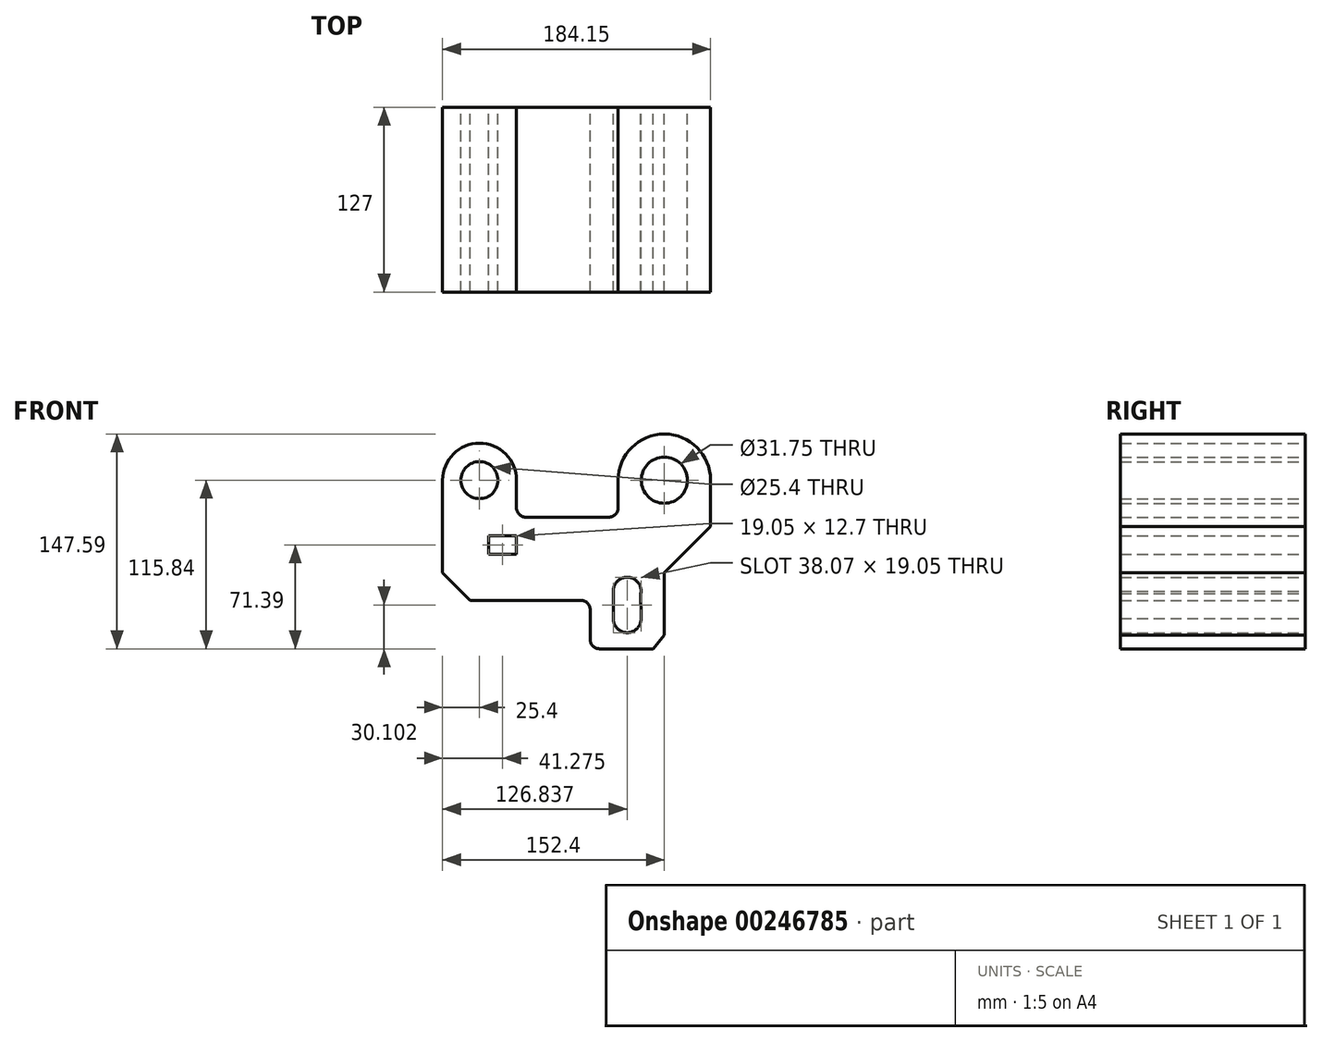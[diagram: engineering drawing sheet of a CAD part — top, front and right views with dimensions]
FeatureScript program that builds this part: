
annotation { "Feature Type Name" : "Feature", "Feature Type Description" : "" }
export const myFeature = defineFeature(function(context is Context, id is Id, definition is map)
    precondition{}
    {
        {
            var Q0;
            Q0=qCreatedBy(makeId("Front.planeOp"),FACE);
            var sketch = newSketch(context, id + "F0", { "sketchPlane" : qUnion([Q0])});
            skCircle(sketch, "E0", {"center": v(0, 0) * mm, "radius": 15.88 * mm});
            skArc(sketch, "E1", {"start": v(31.75, 0) * mm, "mid": v(0, 31.75) * mm, "end": v(-31.75, 0) * mm});
            skLineSegment(sketch, "E2", {"start": v(31.75, 0) * mm, "end": v(31.75, -31.75) * mm});
            skLineSegment(sketch, "E3", {"start": v(31.75, -31.75) * mm, "end": v(62.44, -31.75) * mm, "construction": true});
            skLineSegment(sketch, "E4", {"start": v(0, 0) * mm, "end": v(63.42, 0) * mm, "construction": true});
            skLineSegment(sketch, "E5", {"start": v(70.44, -114.3) * mm, "end": v(0, -114.3) * mm, "construction": true});
            skLineSegment(sketch, "E6", {"start": v(84.52, -63.5) * mm, "end": v(0, -63.5) * mm, "construction": true});
            skArc(sketch, "E7", {"start": v(-101.6, 0) * mm, "mid": v(-127, 25.4) * mm, "end": v(-152.4, 0) * mm});
            skCircle(sketch, "E8", {"center": v(-127, 0) * mm, "radius": 12.7 * mm});
            skLineSegment(sketch, "E9", {"start": v(-95.25, -25.4) * mm, "end": v(-38.1, -25.4) * mm});
            skLineSegment(sketch, "E10", {"start": v(-101.6, 0) * mm, "end": v(-101.6, -19.05) * mm});
            skLineSegment(sketch, "E11", {"start": v(-31.75, 0) * mm, "end": v(-31.75, -19.05) * mm});
            skLineSegment(sketch, "E12", {"start": v(31.75, -31.75) * mm, "end": v(-0.04, -63.54) * mm});
            skPoint(sketch, "E13.visualSharp", {"position": v(-31.75, -25.4) * mm});
            skArc(sketch, "E13.filletArc", {"start": v(-38.1, -25.4) * mm, "mid": v(-33.6, -23.54) * mm, "end": v(-31.75, -19.05) * mm});
            skPoint(sketch, "E14.visualSharp", {"position": v(-101.6, -25.4) * mm});
            skArc(sketch, "E14.filletArc", {"start": v(-101.6, -19.05) * mm, "mid": v(-99.74, -23.54) * mm, "end": v(-95.25, -25.4) * mm});
            skLineSegment(sketch, "E15", {"start": v(-152.4, 0) * mm, "end": v(-152.4, -137.42) * mm, "construction": true});
            skLineSegment(sketch, "E16", {"start": v(-133.35, -65.36) * mm, "end": v(-133.35, -137.42) * mm, "construction": true});
            skLineSegment(sketch, "E17", {"start": v(-133.35, -82.55) * mm, "end": v(-57.31, -82.55) * mm});
            skLineSegment(sketch, "E18", {"start": v(-50.96, -88.9) * mm, "end": v(-50.96, -109.49) * mm});
            skLineSegment(sketch, "E19", {"start": v(-44.61, -115.84) * mm, "end": v(-7.87, -115.84) * mm});
            skLineSegment(sketch, "E20", {"start": v(-7.87, -115.84) * mm, "end": v(0, -106.43) * mm});
            skLineSegment(sketch, "E21", {"start": v(0, -106.43) * mm, "end": v(0, -63.5) * mm});
            skLineSegment(sketch, "E22", {"start": v(-120.65, -17.78) * mm, "end": v(-120.65, -85.3) * mm, "construction": true});
            skPoint(sketch, "E23.firstSnap0", {"position": v(-123.1, -38.1) * mm});
            skLineSegment(sketch, "E23.bottom", {"start": v(-120.65, -38.1) * mm, "end": v(-101.6, -38.1) * mm});
            skLineSegment(sketch, "E23.top", {"start": v(-120.65, -50.8) * mm, "end": v(-101.6, -50.8) * mm});
            skLineSegment(sketch, "E23.left", {"start": v(-120.65, -38.1) * mm, "end": v(-120.65, -50.8) * mm});
            skLineSegment(sketch, "E23.right", {"start": v(-101.6, -38.1) * mm, "end": v(-101.6, -50.8) * mm});
            skPoint(sketch, "E24.startSnap0", {"position": v(-50.96, -99.2) * mm});
            skLineSegment(sketch, "E25", {"start": v(-152.4, -134.23) * mm, "end": v(0, -134.23) * mm, "construction": true});
            skArc(sketch, "E26", {"start": v(-35.09, -95.1) * mm, "mid": v(-25.6, -104.77) * mm, "end": v(-16.04, -95.18) * mm});
            skArc(sketch, "E27", {"start": v(-16.17, -77.76) * mm, "mid": v(-24.85, -66.7) * mm, "end": v(-35.09, -76.35) * mm});
            skLineSegment(sketch, "E28", {"start": v(-16.2, -74.5) * mm, "end": v(-16.04, -95.25) * mm});
            skLineSegment(sketch, "E29", {"start": v(-35.09, -76.35) * mm, "end": v(-35.09, -95.4) * mm});
            skPoint(sketch, "E30.visualSharp", {"position": v(-50.96, -82.55) * mm});
            skArc(sketch, "E30.filletArc", {"start": v(-50.96, -88.9) * mm, "mid": v(-52.82, -84.4) * mm, "end": v(-57.31, -82.55) * mm});
            skPoint(sketch, "E31.visualSharp", {"position": v(-50.96, -115.84) * mm});
            skArc(sketch, "E31.filletArc", {"start": v(-50.96, -109.49) * mm, "mid": v(-49.1, -113.98) * mm, "end": v(-44.61, -115.84) * mm});
            skLineSegment(sketch, "E32", {"start": v(-152.4, 0) * mm, "end": v(-152.4, -63.5) * mm});
            skLineSegment(sketch, "E33", {"start": v(-152.4, -63.5) * mm, "end": v(-133.35, -82.55) * mm});
            skSolve(sketch);
        }
        {
            var Q0;
            Q0=makeQuery(id+"F0.imprint","IMPRINT",FACE,{"disambiguationData":[TD([[makeQuery(id+"F0.imprint","IMPRINT",EDGE,{"derivedFrom":sQuery(id+"F0.wireOp",EDGE,"E0")}),-1.0]])]});
            extrude(context, id + "F1", {"entities" : qUnion([Q0]), "depth" : 127 * mm});
        }
    });
